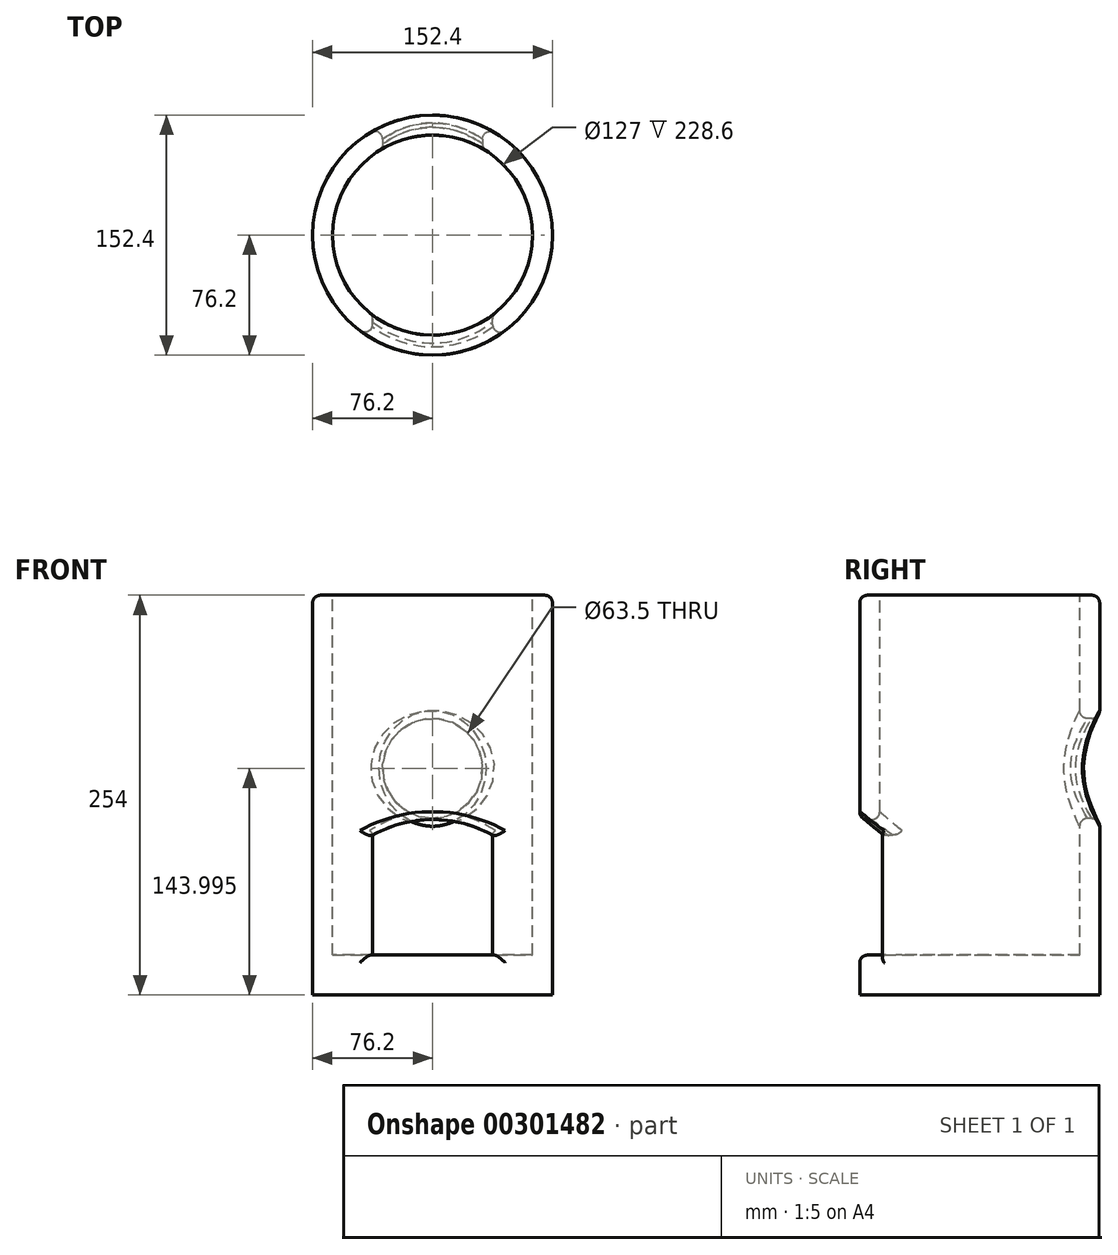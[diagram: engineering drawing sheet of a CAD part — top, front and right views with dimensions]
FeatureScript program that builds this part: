
annotation { "Feature Type Name" : "Feature", "Feature Type Description" : "" }
export const myFeature = defineFeature(function(context is Context, id is Id, definition is map)
    precondition{}
    {
        {
            var Q0;
            Q0=qCreatedBy(makeId("Front.planeOp"),FACE);
            var sketch = newSketch(context, id + "F0", { "sketchPlane" : qUnion([Q0])});
            skLineSegment(sketch, "E0", {"start": v(0, 233.4) * mm, "end": v(-76.2, 233.4) * mm});
            skLineSegment(sketch, "E1", {"start": v(-76.2, 233.4) * mm, "end": v(-76.2, -20.6) * mm});
            skLineSegment(sketch, "E2", {"start": v(-76.2, -20.6) * mm, "end": v(0, -20.6) * mm});
            skLineSegment(sketch, "E3", {"start": v(0, 233.4) * mm, "end": v(0, -20.6) * mm});
            skSolve(sketch);
        }
        {
            var Q0;
            Q0 = qSketchRegion(id + "F0", true);
            var Q1;
            Q1=sQuery(id+"F0.wireOp",EDGE,"E3");
            revolve(context, id + "F1", {"entities" : qUnion([Q0]), "axis" : qUnion([Q1]), "revolveType" : RevolveType.FULL});
        }
        {
            var Q0;
            Q0=qCreatedBy(makeId("Front.planeOp"),FACE);
            var sketch = newSketch(context, id + "F2", { "sketchPlane" : qUnion([Q0])});
            skLineSegment(sketch, "E4", {"start": v(-38.1, 4.8) * mm, "end": v(38.1, 4.8) * mm});
            skLineSegment(sketch, "E5", {"start": v(38.1, 4.8) * mm, "end": v(38.1, 81) * mm});
            skLineSegment(sketch, "E6", {"start": v(-38.1, 4.8) * mm, "end": v(-38.1, 81) * mm});
            skArc(sketch, "E7", {"start": v(38.1, 81) * mm, "mid": v(0, 90.91) * mm, "end": v(-38.1, 81) * mm});
            skLineSegment(sketch, "E8", {"start": v(0, 4.8) * mm, "end": v(0, -20.6) * mm, "construction": true});
            skSolve(sketch);
        }
        {
            var Q0;
            Q0 = qSketchRegion(id + "F2", true);
            extrude(context, id + "F3", {"entities" : qUnion([Q0]), "operationType" : NewBodyOperationType.REMOVE, "depth" : 76.2 * mm});
        }
        {
            var Q0;
            Q0=makeQuery(id+"F1.opRevolve","SWEPT_FACE",FACE,{"disambiguationData":[OSD([sQuery(id+"F0.wireOp",EDGE,"E0")])]});
            var sketch = newSketch(context, id + "F4", { "sketchPlane" : qUnion([Q0])});
            skCircle(sketch, "E9", {"center": v(0, 0) * mm, "radius": 63.5 * mm});
            skSolve(sketch);
        }
        {
            var Q0;
            Q0=makeQuery(id+"F4.imprint","IMPRINT",FACE,{"disambiguationData":[TD([[makeQuery(id+"F4.imprint","IMPRINT",EDGE,{"derivedFrom":sQuery(id+"F4.wireOp",EDGE,"E9")}),1.0]])]});
            extrude(context, id + "F5", {"entities" : qUnion([Q0]), "operationType" : NewBodyOperationType.REMOVE, "oppositeDirection" : true, "depth" : 228.6 * mm});
        }
        {
            var Q0;
            Q0 = qSketchRegion(id + "F2", true);
            extrude(context, id + "F6", {"entities" : qUnion([Q0]), "operationType" : NewBodyOperationType.REMOVE, "oppositeDirection" : true, "depth" : 50.8 * mm});
        }
        {
            var Q0;
            Q0=qCreatedBy(makeId("Front.planeOp"),FACE);
            var sketch = newSketch(context, id + "F7", { "sketchPlane" : qUnion([Q0])});
            skCircle(sketch, "E10", {"center": v(0, 123.4) * mm, "radius": 31.75 * mm});
            skLineSegment(sketch, "E11", {"start": v(0, 233.4) * mm, "end": v(0, 123.4) * mm, "construction": true});
            skSolve(sketch);
        }
        {
            var Q0;
            Q0 = qSketchRegion(id + "F7", true);
            extrude(context, id + "F8", {"entities" : qUnion([Q0]), "operationType" : NewBodyOperationType.REMOVE, "oppositeDirection" : true, "depth" : 76.2 * mm});
        }
        {
            var Q0;
            Q0=makeQuery(id+"F5.boolean.opBoolean","COPY",EDGE,{"derivedFrom":makeQuery(id+"F5.opExtrude","CAP_EDGE",EDGE,{"disambiguationData":[OSD([sQuery(id+"F4.wireOp",EDGE,"E9")])],"isStart":true})});
            var Q1;
            Q1=makeQuery(id+"F1.opRevolve","SWEPT_EDGE",EDGE,{"disambiguationData":[OSD([sQuery(id+"F0.wireOp",EDGE,"E0"),sQuery(id+"F0.wireOp",EDGE,"E1")])]});
            var Q2;
            Q2=makeQuery(id+"F3.boolean.opBoolean","INTERSECT",EDGE,{"derivedFrom":[makeQuery(id+"F1.opRevolve","SWEPT_FACE",FACE,{"disambiguationData":[OSD([sQuery(id+"F0.wireOp",EDGE,"E1")])]}),makeQuery(id+"F3.opExtrude","SWEPT_FACE",FACE,{"disambiguationData":[OSD([sQuery(id+"F2.wireOp",EDGE,"E6")])]})]});
            var Q3;
            Q3=makeQuery(id+"F3.boolean.opBoolean","INTERSECT",EDGE,{"derivedFrom":[makeQuery(id+"F1.opRevolve","SWEPT_FACE",FACE,{"disambiguationData":[OSD([sQuery(id+"F0.wireOp",EDGE,"E1")])]}),makeQuery(id+"F3.opExtrude","SWEPT_FACE",FACE,{"disambiguationData":[OSD([sQuery(id+"F2.wireOp",EDGE,"E7")])]})]});
            var Q4;
            Q4=makeQuery(id+"F3.boolean.opBoolean","INTERSECT",EDGE,{"derivedFrom":[makeQuery(id+"F1.opRevolve","SWEPT_FACE",FACE,{"disambiguationData":[OSD([sQuery(id+"F0.wireOp",EDGE,"E1")])]}),makeQuery(id+"F3.opExtrude","SWEPT_FACE",FACE,{"disambiguationData":[OSD([sQuery(id+"F2.wireOp",EDGE,"E5")])]})]});
            var Q5;
            Q5=makeQuery(id+"F3.boolean.opBoolean","INTERSECT",EDGE,{"derivedFrom":[makeQuery(id+"F1.opRevolve","SWEPT_FACE",FACE,{"disambiguationData":[OSD([sQuery(id+"F0.wireOp",EDGE,"E1")])]}),makeQuery(id+"F3.opExtrude","SWEPT_FACE",FACE,{"disambiguationData":[OSD([sQuery(id+"F2.wireOp",EDGE,"E4")])]})]});
            var Q6;
            Q6=makeQuery(id+"F5.boolean.opBoolean","INTERSECT",EDGE,{"derivedFrom":[makeQuery(id+"F3.boolean.opBoolean","COPY",FACE,{"derivedFrom":makeQuery(id+"F3.opExtrude","SWEPT_FACE",FACE,{"disambiguationData":[OSD([sQuery(id+"F2.wireOp",EDGE,"E6")])]})}),makeQuery(id+"F5.opExtrude","SWEPT_FACE",FACE,{"disambiguationData":[OSD([sQuery(id+"F4.wireOp",EDGE,"E9")])]})]});
            var Q7;
            Q7=makeQuery(id+"F5.boolean.opBoolean","INTERSECT",EDGE,{"derivedFrom":[makeQuery(id+"F3.boolean.opBoolean","COPY",FACE,{"derivedFrom":makeQuery(id+"F3.opExtrude","SWEPT_FACE",FACE,{"disambiguationData":[OSD([sQuery(id+"F2.wireOp",EDGE,"E5")])]})}),makeQuery(id+"F5.opExtrude","SWEPT_FACE",FACE,{"disambiguationData":[OSD([sQuery(id+"F4.wireOp",EDGE,"E9")])]})]});
            var Q8;
            Q8=makeQuery(id+"F5.boolean.opBoolean","INTERSECT",EDGE,{"derivedFrom":[makeQuery(id+"F3.boolean.opBoolean","COPY",FACE,{"derivedFrom":makeQuery(id+"F3.opExtrude","SWEPT_FACE",FACE,{"disambiguationData":[OSD([sQuery(id+"F2.wireOp",EDGE,"E7")])]})}),makeQuery(id+"F5.opExtrude","SWEPT_FACE",FACE,{"disambiguationData":[OSD([sQuery(id+"F4.wireOp",EDGE,"E9")])]})]});
            var Q9;
            Q9=makeQuery(id+"F8.boolean.opBoolean","INTERSECT",EDGE,{"derivedFrom":[makeQuery(id+"F5.boolean.opBoolean","COPY",FACE,{"derivedFrom":makeQuery(id+"F5.opExtrude","SWEPT_FACE",FACE,{"disambiguationData":[OSD([sQuery(id+"F4.wireOp",EDGE,"E9")])]})}),makeQuery(id+"F8.opExtrude","SWEPT_FACE",FACE,{"disambiguationData":[OSD([sQuery(id+"F7.wireOp",EDGE,"E10")])]})]});
            var Q10;
            Q10=makeQuery(id+"F8.boolean.opBoolean","INTERSECT",EDGE,{"derivedFrom":[makeQuery(id+"F1.opRevolve","SWEPT_FACE",FACE,{"disambiguationData":[OSD([sQuery(id+"F0.wireOp",EDGE,"E1")])]}),makeQuery(id+"F8.opExtrude","SWEPT_FACE",FACE,{"disambiguationData":[OSD([sQuery(id+"F7.wireOp",EDGE,"E10")])]})]});
            fillet(context, id + "F9", {"entities" : qUnion([Q0, Q1, Q2, Q3, Q4, Q5, Q6, Q7, Q8, Q9, Q10]), "radius" : 5 * mm, "tangentPropagation" : true, "allowEdgeOverflow" : false});
        }
    });
